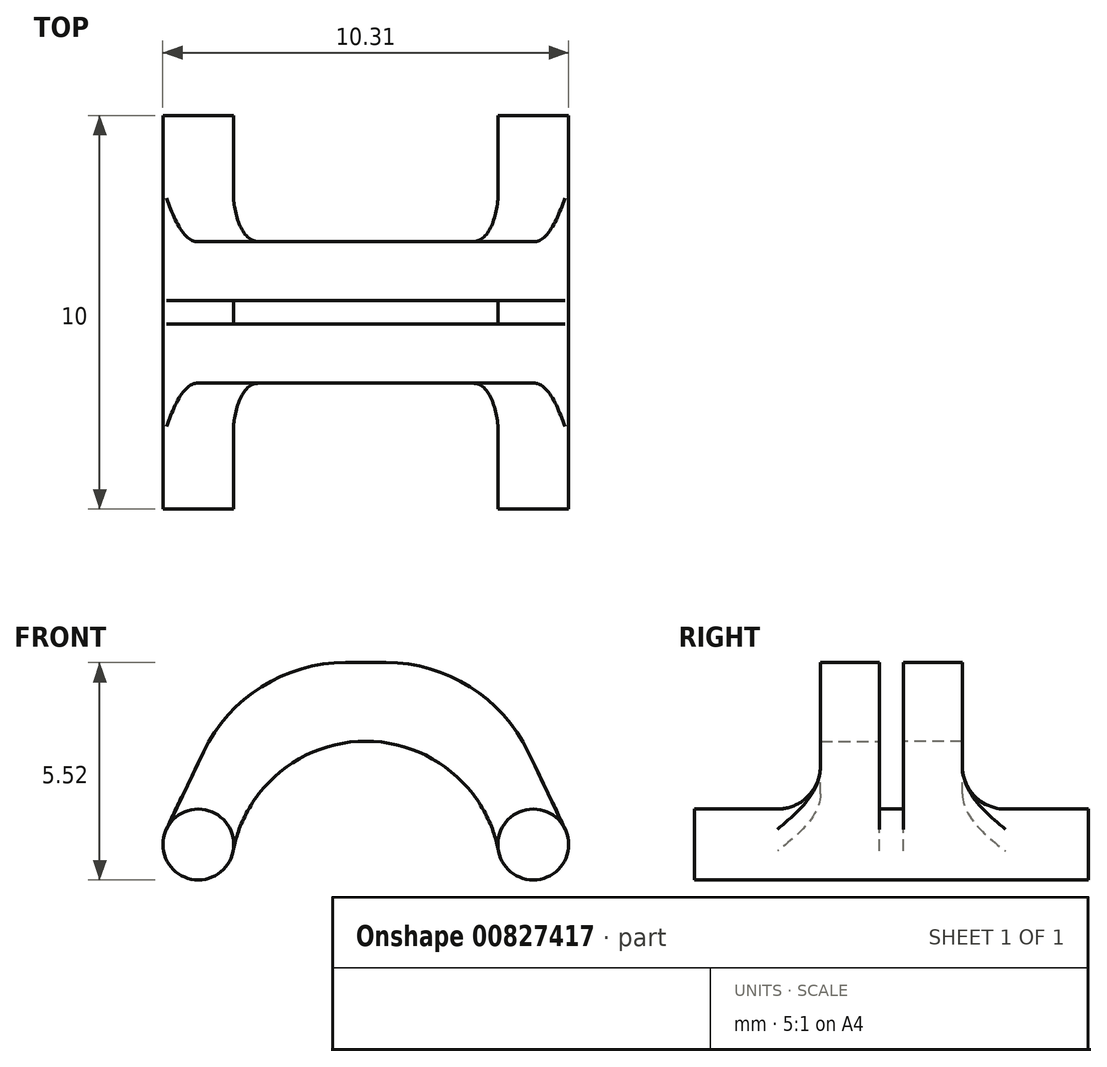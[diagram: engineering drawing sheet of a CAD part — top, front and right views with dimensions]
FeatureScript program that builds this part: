
annotation { "Feature Type Name" : "Feature", "Feature Type Description" : "" }
export const myFeature = defineFeature(function(context is Context, id is Id, definition is map)
    precondition{}
    {
        {
            var Q0;
            Q0=qCreatedBy(makeId("Front.planeOp"),FACE);
            var sketch = newSketch(context, id + "F0", { "sketchPlane" : qUnion([Q0])});
            skCircle(sketch, "E0", {"center": v(-16.68, 0) * mm, "radius": 0.9 * mm});
            skCircle(sketch, "E1", {"center": v(-8.17, 0) * mm, "radius": 0.9 * mm});
            skSolve(sketch);
        }
        {
            var Q0;
            Q0=makeQuery(id+"F0.imprint","IMPRINT",FACE,{"disambiguationData":[TD([[makeQuery(id+"F0.imprint","IMPRINT",EDGE,{"derivedFrom":sQuery(id+"F0.wireOp",EDGE,"E0")}),1.0]])]});
            var Q1;
            Q1=makeQuery(id+"F0.imprint","IMPRINT",FACE,{"disambiguationData":[TD([[makeQuery(id+"F0.imprint","IMPRINT",EDGE,{"derivedFrom":sQuery(id+"F0.wireOp",EDGE,"E1")}),1.0]])]});
            extrude(context, id + "F1", {"entities" : qUnion([Q0, Q1]), "depth" : 10 * mm, "offsetDistance" : 25 * mm});
        }
        {
            var Q0;
            Q0=qCreatedBy(makeId("Front.planeOp"),FACE);
            cPlane(context, id + "F2", {"entities" : qUnion([Q0]), "cplaneType" : CPlaneType.OFFSET, "offset" : 5 * mm, "width" : 150 * mm, "height" : 150 * mm});
        }
        {
            var Q0;
            Q0=qCreatedBy(id+"F2.planeOp",FACE);
            cPlane(context, id + "F3", {"entities" : qUnion([Q0]), "cplaneType" : CPlaneType.OFFSET, "offset" : 0.3 * mm, "width" : 150 * mm, "height" : 150 * mm});
        }
        {
            var Q0;
            Q0=qCreatedBy(id+"F2.planeOp",FACE);
            cPlane(context, id + "F4", {"entities" : qUnion([Q0]), "cplaneType" : CPlaneType.OFFSET, "offset" : 0.3 * mm, "oppositeDirection" : true, "width" : 150 * mm, "height" : 150 * mm});
        }
        {
            var Q0;
            Q0=qCreatedBy(id+"F3.planeOp",FACE);
            var sketch = newSketch(context, id + "F5", { "sketchPlane" : qUnion([Q0])});
            skCircle(sketch, "E2.0.0", {"center": v(-16.68, 0) * mm, "radius": 0.9 * mm, "construction": true});
            skCircle(sketch, "E3.0.0", {"center": v(-8.17, 0) * mm, "radius": 0.9 * mm, "construction": true});
            skLineSegment(sketch, "E4", {"start": v(-16.68, 0) * mm, "end": v(-8.17, 0) * mm, "construction": true});
            skPoint(sketch, "E5", {"position": v(-12.42, 0) * mm});
            skLineSegment(sketch, "E6", {"start": v(-12.94, 4.62) * mm, "end": v(-11.9, 4.62) * mm});
            skPoint(sketch, "E7", {"position": v(-12.42, 4.62) * mm});
            skLineSegment(sketch, "E8", {"start": v(-16.55, 2.35) * mm, "end": v(-17.49, 0.39) * mm});
            skLineSegment(sketch, "E9", {"start": v(-8.3, 2.35) * mm, "end": v(-7.36, 0.39) * mm});
            skPoint(sketch, "E10", {"position": v(-12.42, -0.8) * mm});
            skLineSegment(sketch, "E11", {"start": v(-16.68, 0) * mm, "end": v(-12.42, -0.8) * mm, "construction": true});
            skArc(sketch, "E12", {"start": v(-15.8, -0.17) * mm, "mid": v(-12.42, 2.62) * mm, "end": v(-9.05, -0.17) * mm});
            skPoint(sketch, "E13.visualSharp", {"position": v(-15.46, 4.62) * mm});
            skArc(sketch, "E13.filletArc", {"start": v(-12.94, 4.62) * mm, "mid": v(-15.07, 4) * mm, "end": v(-16.55, 2.35) * mm});
            skPoint(sketch, "E14.visualSharp", {"position": v(-9.39, 4.62) * mm});
            skArc(sketch, "E14.filletArc", {"start": v(-8.3, 2.35) * mm, "mid": v(-9.78, 4) * mm, "end": v(-11.9, 4.62) * mm});
            skLineSegment(sketch, "E15", {"start": v(-17.49, 0.39) * mm, "end": v(-15.8, -0.17) * mm});
            skLineSegment(sketch, "E16", {"start": v(-9.05, -0.17) * mm, "end": v(-7.36, 0.39) * mm});
            skSolve(sketch);
        }
        {
            var Q0;
            Q0=makeQuery(id+"F5.imprint","IMPRINT",FACE,{"disambiguationData":[TD([[makeQuery(id+"F5.imprint","IMPRINT",EDGE,{"derivedFrom":sQuery(id+"F5.wireOp",EDGE,"E6")}),-1.0]])]});
            extrude(context, id + "F6", {"entities" : qUnion([Q0]), "depth" : 1.5 * mm, "offsetDistance" : 25 * mm});
        }
        {
            var Q0;
            Q0=qCreatedBy(id+"F4.planeOp",FACE);
            var sketch = newSketch(context, id + "F7", { "sketchPlane" : qUnion([Q0])});
            skLineSegment(sketch, "E17.0.0", {"start": v(-15.8, -0.17) * mm, "end": v(-17.49, 0.39) * mm});
            skLineSegment(sketch, "E17.0.1", {"start": v(-17.49, 0.39) * mm, "end": v(-16.55, 2.35) * mm});
            skArc(sketch, "E17.0.2", {"start": v(-16.55, 2.35) * mm, "mid": v(-15.07, 4) * mm, "end": v(-12.94, 4.62) * mm});
            skLineSegment(sketch, "E17.0.3", {"start": v(-12.94, 4.62) * mm, "end": v(-11.9, 4.62) * mm});
            skArc(sketch, "E17.0.4", {"start": v(-11.9, 4.62) * mm, "mid": v(-9.78, 4) * mm, "end": v(-8.3, 2.35) * mm});
            skLineSegment(sketch, "E17.0.5", {"start": v(-8.3, 2.35) * mm, "end": v(-7.36, 0.39) * mm});
            skLineSegment(sketch, "E17.0.6", {"start": v(-7.36, 0.39) * mm, "end": v(-9.05, -0.17) * mm});
            skArc(sketch, "E17.0.7", {"start": v(-9.05, -0.17) * mm, "mid": v(-12.42, 2.62) * mm, "end": v(-15.8, -0.17) * mm});
            skSolve(sketch);
        }
        {
            var Q0;
            Q0=makeQuery(id+"F7.imprint","IMPRINT",FACE,{"disambiguationData":[TD([[makeQuery(id+"F7.imprint","IMPRINT",EDGE,{"derivedFrom":sQuery(id+"F7.wireOp",EDGE,"E17.0.0")}),-1.0]])]});
            extrude(context, id + "F8", {"entities" : qUnion([Q0]), "oppositeDirection" : true, "depth" : 1.5 * mm, "offsetDistance" : 25 * mm});
        }
        {
            var Q0;
            Q0=makeQuery(id+"F1.opExtrude","SWEPT_BODY",BODY,{"disambiguationData":[OSD([sQuery(id+"F0.wireOp",EDGE,"E0")])]});
            var Q1;
            Q1=makeQuery(id+"F1.opExtrude","SWEPT_BODY",BODY,{"disambiguationData":[OSD([sQuery(id+"F0.wireOp",EDGE,"E1")])]});
            var Q2;
            Q2=makeQuery(id+"F6.opExtrude","SWEPT_BODY",BODY,{"disambiguationData":[OSD([sQuery(id+"F5.wireOp",EDGE,"E6"),sQuery(id+"F5.wireOp",EDGE,"E8"),sQuery(id+"F5.wireOp",EDGE,"E9"),sQuery(id+"F5.wireOp",EDGE,"E12"),sQuery(id+"F5.wireOp",EDGE,"E13.filletArc"),sQuery(id+"F5.wireOp",EDGE,"E14.filletArc"),sQuery(id+"F5.wireOp",EDGE,"E15"),sQuery(id+"F5.wireOp",EDGE,"E16")])]});
            var Q3;
            Q3=makeQuery(id+"F8.opExtrude","SWEPT_BODY",BODY,{"disambiguationData":[OSD([sQuery(id+"F7.wireOp",EDGE,"E17.0.0"),sQuery(id+"F7.wireOp",EDGE,"E17.0.1"),sQuery(id+"F7.wireOp",EDGE,"E17.0.2"),sQuery(id+"F7.wireOp",EDGE,"E17.0.3"),sQuery(id+"F7.wireOp",EDGE,"E17.0.4"),sQuery(id+"F7.wireOp",EDGE,"E17.0.5"),sQuery(id+"F7.wireOp",EDGE,"E17.0.6"),sQuery(id+"F7.wireOp",EDGE,"E17.0.7")])]});
            booleanBodies(context, id + "F9", {"operationType" : BooleanOperationType.UNION, "tools" : qUnion([Q0, Q1, Q2, Q3])});
        }
        {
            var Q0;
            Q0=makeQuery(id+"F9.opBoolean","INTERSECT",EDGE,{"derivedFrom":[makeQuery(id+"F1.opExtrude","SWEPT_FACE",FACE,{"disambiguationData":[OSD([sQuery(id+"F0.wireOp",EDGE,"E1")])]}),makeQuery(id+"F6.opExtrude","CAP_FACE",FACE,{"disambiguationData":[OSD([sQuery(id+"F5.wireOp",EDGE,"E6"),sQuery(id+"F5.wireOp",EDGE,"E8"),sQuery(id+"F5.wireOp",EDGE,"E9"),sQuery(id+"F5.wireOp",EDGE,"E12"),sQuery(id+"F5.wireOp",EDGE,"E13.filletArc"),sQuery(id+"F5.wireOp",EDGE,"E14.filletArc"),sQuery(id+"F5.wireOp",EDGE,"E15"),sQuery(id+"F5.wireOp",EDGE,"E16")])],"isStart":false})]});
            var Q1;
            Q1=makeQuery(id+"F9.opBoolean","INTERSECT",EDGE,{"derivedFrom":[makeQuery(id+"F1.opExtrude","SWEPT_FACE",FACE,{"disambiguationData":[OSD([sQuery(id+"F0.wireOp",EDGE,"E1")])]}),makeQuery(id+"F8.opExtrude","CAP_FACE",FACE,{"disambiguationData":[OSD([sQuery(id+"F7.wireOp",EDGE,"E17.0.0"),sQuery(id+"F7.wireOp",EDGE,"E17.0.1"),sQuery(id+"F7.wireOp",EDGE,"E17.0.2"),sQuery(id+"F7.wireOp",EDGE,"E17.0.3"),sQuery(id+"F7.wireOp",EDGE,"E17.0.4"),sQuery(id+"F7.wireOp",EDGE,"E17.0.5"),sQuery(id+"F7.wireOp",EDGE,"E17.0.6"),sQuery(id+"F7.wireOp",EDGE,"E17.0.7")])],"isStart":false})]});
            var Q2;
            Q2=makeQuery(id+"F9.opBoolean","INTERSECT",EDGE,{"derivedFrom":[makeQuery(id+"F1.opExtrude","SWEPT_FACE",FACE,{"disambiguationData":[OSD([sQuery(id+"F0.wireOp",EDGE,"E0")])]}),makeQuery(id+"F8.opExtrude","CAP_FACE",FACE,{"disambiguationData":[OSD([sQuery(id+"F7.wireOp",EDGE,"E17.0.0"),sQuery(id+"F7.wireOp",EDGE,"E17.0.1"),sQuery(id+"F7.wireOp",EDGE,"E17.0.2"),sQuery(id+"F7.wireOp",EDGE,"E17.0.3"),sQuery(id+"F7.wireOp",EDGE,"E17.0.4"),sQuery(id+"F7.wireOp",EDGE,"E17.0.5"),sQuery(id+"F7.wireOp",EDGE,"E17.0.6"),sQuery(id+"F7.wireOp",EDGE,"E17.0.7")])],"isStart":false})]});
            var Q3;
            Q3=makeQuery(id+"F9.opBoolean","INTERSECT",EDGE,{"derivedFrom":[makeQuery(id+"F1.opExtrude","SWEPT_FACE",FACE,{"disambiguationData":[OSD([sQuery(id+"F0.wireOp",EDGE,"E0")])]}),makeQuery(id+"F6.opExtrude","CAP_FACE",FACE,{"disambiguationData":[OSD([sQuery(id+"F5.wireOp",EDGE,"E6"),sQuery(id+"F5.wireOp",EDGE,"E8"),sQuery(id+"F5.wireOp",EDGE,"E9"),sQuery(id+"F5.wireOp",EDGE,"E12"),sQuery(id+"F5.wireOp",EDGE,"E13.filletArc"),sQuery(id+"F5.wireOp",EDGE,"E14.filletArc"),sQuery(id+"F5.wireOp",EDGE,"E15"),sQuery(id+"F5.wireOp",EDGE,"E16")])],"isStart":false})]});
            fillet(context, id + "F10", {"entities" : qUnion([Q0, Q1, Q2, Q3]), "tangentPropagation" : true, "radius" : 1.1 * mm, "defaultsChanged" : true, "vertexSettings" : [], "allowEdgeOverflow" : false});
        }
    });
